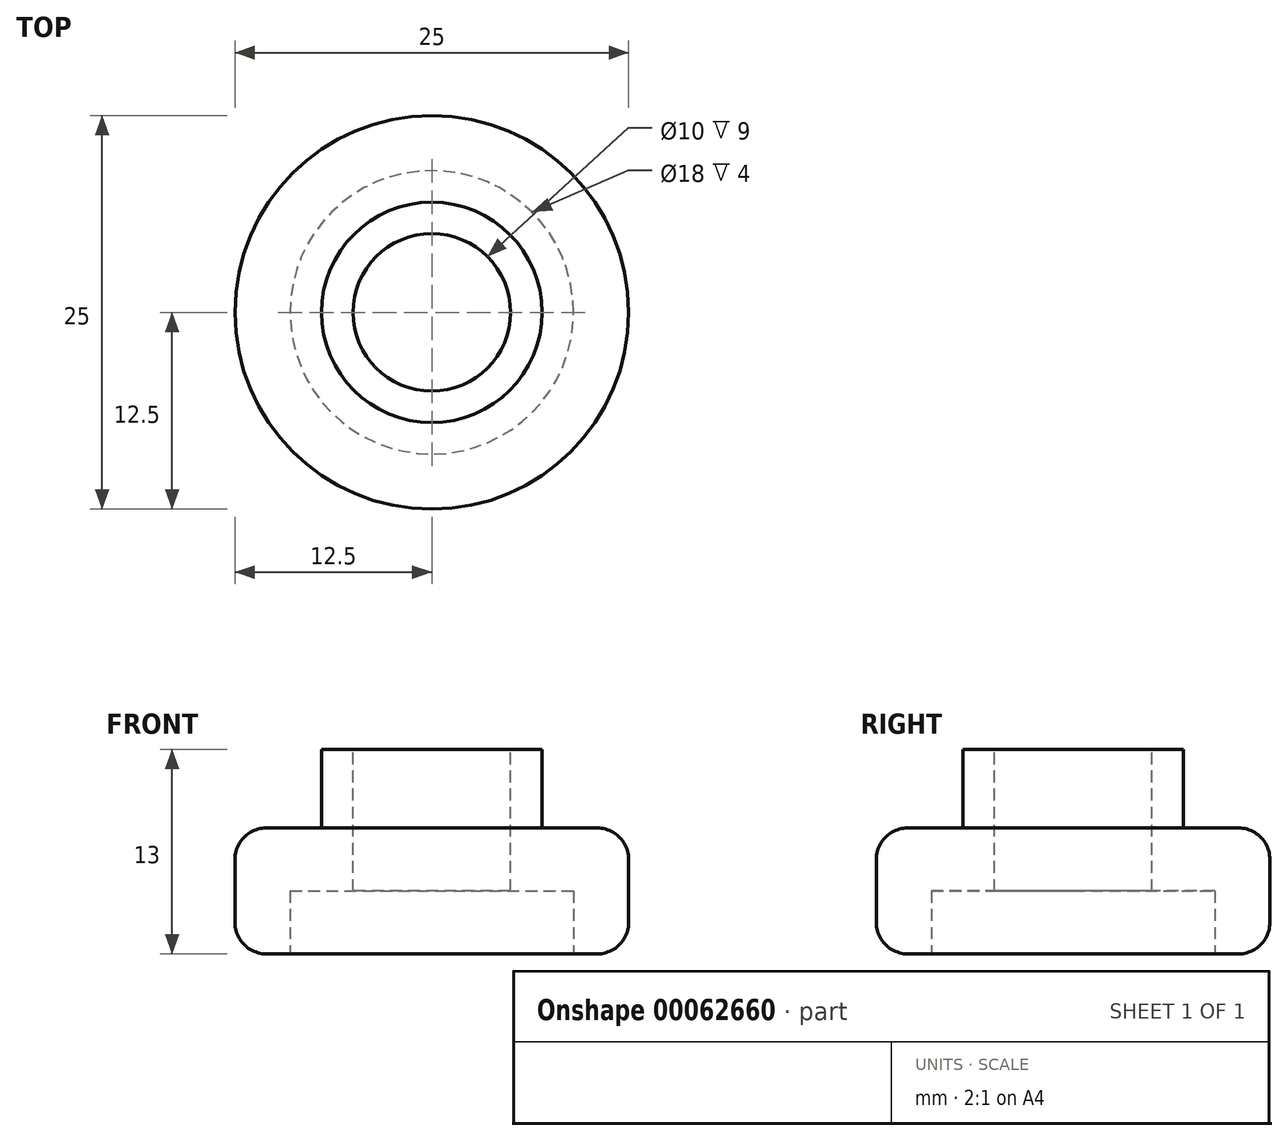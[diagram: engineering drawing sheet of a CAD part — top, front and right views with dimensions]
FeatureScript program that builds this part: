
annotation { "Feature Type Name" : "Feature", "Feature Type Description" : "" }
export const myFeature = defineFeature(function(context is Context, id is Id, definition is map)
    precondition{}
    {
        {
            var Q0;
            Q0=qCreatedBy(makeId("Top.planeOp"),FACE);
            var sketch = newSketch(context, id + "F0", { "sketchPlane" : qUnion([Q0])});
            skCircle(sketch, "E0", {"center": v(0, 0) * mm, "radius": 12.5 * mm});
            skSolve(sketch);
        }
        {
            var Q0;
            Q0 = qSketchRegion(id + "F0", true);
            extrude(context, id + "F1", {"entities" : qUnion([Q0]), "depth" : 8 * mm});
        }
        {
            var Q0;
            Q0=makeQuery(id+"F1.opExtrude","CAP_FACE",FACE,{"disambiguationData":[OSD([sQuery(id+"F0.wireOp",EDGE,"E0")])],"isStart":false});
            var sketch = newSketch(context, id + "F2", { "sketchPlane" : qUnion([Q0])});
            skCircle(sketch, "E1", {"center": v(0, 0) * mm, "radius": 7 * mm});
            skSolve(sketch);
        }
        {
            var Q0;
            Q0 = qSketchRegion(id + "F2", true);
            extrude(context, id + "F3", {"entities" : qUnion([Q0]), "operationType" : NewBodyOperationType.ADD, "depth" : 5 * mm});
        }
        {
            var Q0;
            Q0=makeQuery(id+"F3.opExtrude","CAP_FACE",FACE,{"disambiguationData":[OSD([sQuery(id+"F2.wireOp",EDGE,"E1")])],"isStart":false});
            var sketch = newSketch(context, id + "F4", { "sketchPlane" : qUnion([Q0])});
            skCircle(sketch, "E2", {"center": v(0, 0) * mm, "radius": 5 * mm});
            skSolve(sketch);
        }
        {
            var Q0;
            Q0 = qSketchRegion(id + "F4", true);
            extrude(context, id + "F5", {"entities" : qUnion([Q0]), "operationType" : NewBodyOperationType.REMOVE, "oppositeDirection" : true, "depth" : 25 * mm});
        }
        {
            var Q0;
            Q0=makeQuery(id+"F1.opExtrude","CAP_FACE",FACE,{"disambiguationData":[OSD([sQuery(id+"F0.wireOp",EDGE,"E0")])],"isStart":true});
            var sketch = newSketch(context, id + "F6", { "sketchPlane" : qUnion([Q0])});
            skCircle(sketch, "E3", {"center": v(0, 0) * mm, "radius": 9 * mm});
            skSolve(sketch);
        }
        {
            var Q0;
            Q0=makeQuery(id+"F6.imprint","IMPRINT",FACE,{"disambiguationData":[TD([[makeQuery(id+"F6.imprint","IMPRINT",EDGE,{"derivedFrom":sQuery(id+"F6.wireOp",EDGE,"E3")}),1.0]])]});
            var Q1;
            Q1=sQuery(id+"F6.wireOp",EDGE,"E3");
            extrude(context, id + "F7", {"entities" : qUnion([Q0]), "operationType" : NewBodyOperationType.REMOVE, "surfaceEntities" : qUnion([Q1]), "oppositeDirection" : true, "depth" : 4 * mm});
        }
        {
            var Q0;
            Q0=makeQuery(id+"F1.opExtrude","CAP_EDGE",EDGE,{"disambiguationData":[OSD([sQuery(id+"F0.wireOp",EDGE,"E0")])],"isStart":true});
            var Q1;
            Q1=makeQuery(id+"F1.opExtrude","CAP_EDGE",EDGE,{"disambiguationData":[OSD([sQuery(id+"F0.wireOp",EDGE,"E0")])],"isStart":false});
            fillet(context, id + "F8", {"entities" : qUnion([Q0, Q1]), "radius" : 2 * mm, "tangentPropagation" : true, "allowEdgeOverflow" : false});
        }
    });
